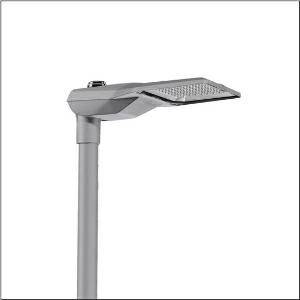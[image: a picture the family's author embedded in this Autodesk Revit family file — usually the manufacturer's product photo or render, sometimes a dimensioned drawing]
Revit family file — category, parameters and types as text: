
# Revit family: streetlight_sl_21_midi___st0_8a_5xe7c37n08mb_215a
name_source: partatom
category: Lighting Fixtures
units: mm (PartAtom-declared; Revit-internal decimal feet)

## family parameters
Cut with Voids When Loaded = No
Host = Face
Light Source = No
Part Type = Normal
Room Calculation Point = No
Round Connector Dimension = Use Diameter
Shared = No

## types (1)
- --- (1 x LED, 18270 lm, 136 W, 3000K)
    Apparent Load = 136 VA
    CIE Flux Codes = 38 75 97 100 100
    Color Rendering = 70
    Color Temperature = 3000K
    Default Elevation = 1800 mm
    Description = Streetlight SL 21 midi, mast luminaire, primary light control with lens, of PMMA, primary optical cover: cover, of toughened safety glass, transparent, light distribution: ST0.8a, light emission: direct distribution, primary light characteristic: asymmetric, installation type: side-entry, LED, 3G 2.5mm², High Power LED, rated luminous flux: 18.270lm, luminous efficacy: 134lm/W, light colour: 730, colour temperature: 3000K, control: overheat protection, presetting dimming linear, constant luminous flux control, time-dependent luminous flux control, flexible luminous flux parameterisation, mains connection: 220..240V, AC, 50/60Hz, connection cable pre-assembled, cable length: 12,5m, wiring characteristics: H05VV-F, start of lifetime: 136W, end of service life: 142W, reduction: 61W, luminaire housing, of diecast aluminium (EN AC-44300), powder-coated, Siteco® metallic grey (DB 702S), corrosivity category C5 mid according to DIN EN ISO 12944, multi-level sealing system, sealing non-destructively replaceable, inclination adjustable: 0°, 5°, 10°, 15°, length: 644mm, width: 335mm, height: 110mm, spigot size: 42mm (side-entry), protection rating (complete): IP66, insulation class (complete): insulation class I (protective earthing), certification: CE, ENEC, ENEC+, VDE, impact resistance: IK09, permissible operating ambient temperature for outdoor applications: -40..+50°C, standard-compliant lighting for roads and squares, packaging unit: 1 piece

Light Distribution: ST0.8a
    Height = 111 mm
    Lamp = 1 x LED
    Lamp Light Flux = 18270 lm
    Lamp Power = 136 W
    Lamp count = 1
    Length = 644 mm
    Luminous efficacy = 134 lm/W
    Manufacturer = Siteco
    ModVariant = No
    Model = 5XE7C37N08MB
    Number of Poles = 1
    OnlyDefault = Yes
    Power Factor = 1
    Product Name = Streetlight SL 21 midi | ST0.8a
    Product group = mast luminaire | pylon top
    ProductGroupID = 6100
    Protection Class = Protection class I
    Protection Degree = IP 66
    RLX_Detail_Level = 1
    RLX_Emergency_Light_Flux = 0 lm
    RLX_Emergency_Type = 0
    RLX_Emergency_Type_DB = No
    RlxData = <blob elided: 90509 chars, md5=c6f96a27>
    Socket = socket
    Standby Power = 0 W
    System Light Flux = 18270 lm
    System Power = 136 W
    Type Comments = factory setting: luminous flux: 100 % | dim-lin: 254 | 695 mA
    Type Image = l_1294377.jpg
    URL = http://relux.com
    VarID = @adj_083447
    Voltage = 0 V
    Weight = 0.00 kg
    Width = 336 mm

## geometry (parser evidence)
native form markers: Blend x4, Sweep x12
no freeform markers — native parametric forms only
